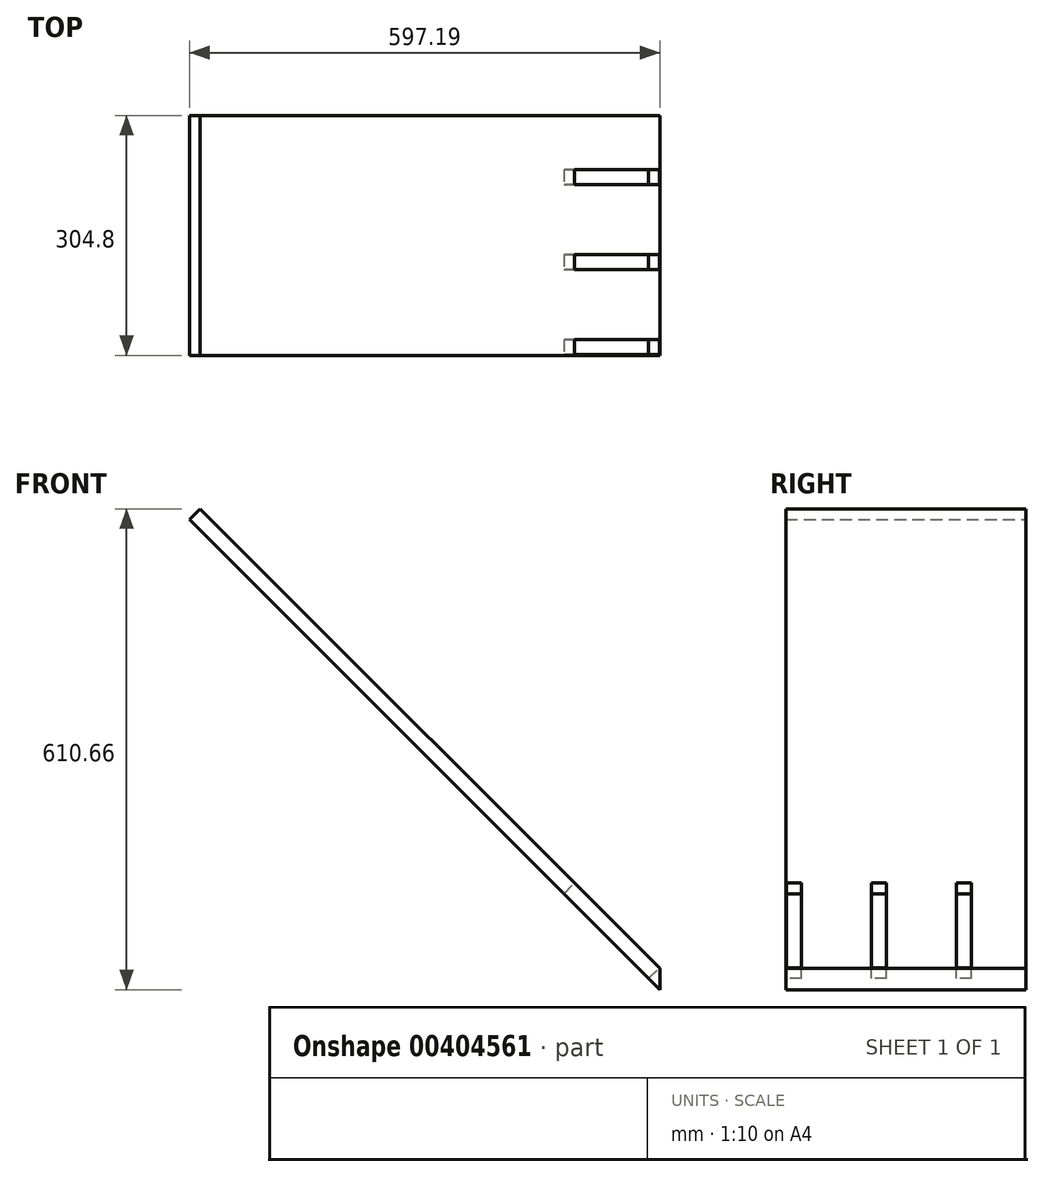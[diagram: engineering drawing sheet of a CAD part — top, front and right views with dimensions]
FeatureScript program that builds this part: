
annotation { "Feature Type Name" : "Feature", "Feature Type Description" : "" }
export const myFeature = defineFeature(function(context is Context, id is Id, definition is map)
    precondition{}
    {
        {
            var Q0;
            Q0=qCreatedBy(makeId("Front.planeOp"),FACE);
            var sketch = newSketch(context, id + "F0", { "sketchPlane" : qUnion([Q0])});
            skLineSegment(sketch, "E0.MirrorCS", {"start": v(378.53, 134.65) * mm, "end": v(-218.66, 731.84) * mm});
            skLineSegment(sketch, "E1.MirrorCS", {"start": v(378.53, 161.6) * mm, "end": v(-205.19, 745.3) * mm});
            skLineSegment(sketch, "E2.MirrorCS", {"start": v(378.53, 134.65) * mm, "end": v(378.53, 161.6) * mm});
            skLineSegment(sketch, "E3", {"start": v(-205.19, 745.3) * mm, "end": v(-218.66, 731.84) * mm});
            skSolve(sketch);
        }
        {
            var Q0;
            Q0=qSketchRegion(id+"F0",true);
            extrude(context, id + "F1", {"entities" : qUnion([Q0]), "endBound" : BoundingType.SYMMETRIC, "depth" : 304.8 * mm});
        }
        {
            var Q0;
            Q0=makeQuery(id+"F1.opExtrude","SWEPT_FACE",FACE,{"disambiguationData":[OSD([sQuery(id+"F0.wireOp",EDGE,"E1.MirrorCS")])]});
            var sketch = newSketch(context, id + "F2", { "sketchPlane" : qUnion([Q0])});
            skLineSegment(sketch, "E4.bottom", {"start": v(83.55, -152.4) * mm, "end": v(64.5, -152.4) * mm});
            skLineSegment(sketch, "E4.top", {"start": v(83.55, 0) * mm, "end": v(64.5, 0) * mm});
            skLineSegment(sketch, "E4.left", {"start": v(83.55, -152.4) * mm, "end": v(83.55, 0) * mm});
            skLineSegment(sketch, "E4.right", {"start": v(64.5, -152.4) * mm, "end": v(64.5, 0) * mm});
            skLineSegment(sketch, "E5.bottom", {"start": v(-24.4, -152.4) * mm, "end": v(-43.45, -152.4) * mm});
            skLineSegment(sketch, "E5.top", {"start": v(-24.4, 0) * mm, "end": v(-43.45, 0) * mm});
            skLineSegment(sketch, "E5.left", {"start": v(-24.4, -152.4) * mm, "end": v(-24.4, 0) * mm});
            skLineSegment(sketch, "E5.right", {"start": v(-43.45, -152.4) * mm, "end": v(-43.45, 0) * mm});
            skLineSegment(sketch, "E6.bottom", {"start": v(-132.35, -152.4) * mm, "end": v(-151.4, -152.4) * mm});
            skLineSegment(sketch, "E6.top", {"start": v(-132.35, 0) * mm, "end": v(-151.4, 0) * mm});
            skLineSegment(sketch, "E6.left", {"start": v(-132.35, -152.4) * mm, "end": v(-132.35, 0) * mm});
            skLineSegment(sketch, "E6.right", {"start": v(-151.4, -152.4) * mm, "end": v(-151.4, 0) * mm});
            skLineSegment(sketch, "E7.bottom", {"start": v(-240.3, -152.4) * mm, "end": v(-259.35, -152.4) * mm});
            skLineSegment(sketch, "E7.top", {"start": v(-240.3, 0) * mm, "end": v(-259.35, 0) * mm});
            skLineSegment(sketch, "E7.left", {"start": v(-240.3, -152.4) * mm, "end": v(-240.3, 0) * mm});
            skLineSegment(sketch, "E7.right", {"start": v(-259.35, -152.4) * mm, "end": v(-259.35, 0) * mm});
            skLineSegment(sketch, "E8.bottom", {"start": v(-348.25, -152.4) * mm, "end": v(-367.3, -152.4) * mm});
            skLineSegment(sketch, "E8.top", {"start": v(-348.25, 0) * mm, "end": v(-367.3, 0) * mm});
            skLineSegment(sketch, "E8.left", {"start": v(-348.25, -152.4) * mm, "end": v(-348.25, 0) * mm});
            skLineSegment(sketch, "E8.right", {"start": v(-367.3, -152.4) * mm, "end": v(-367.3, 0) * mm});
            skLineSegment(sketch, "E9.bottom", {"start": v(-456.2, -152.4) * mm, "end": v(-475.25, -152.4) * mm});
            skLineSegment(sketch, "E9.top", {"start": v(-456.2, 0) * mm, "end": v(-475.25, 0) * mm});
            skLineSegment(sketch, "E9.left", {"start": v(-456.2, -152.4) * mm, "end": v(-456.2, 0) * mm});
            skLineSegment(sketch, "E9.right", {"start": v(-475.25, -152.4) * mm, "end": v(-475.25, 0) * mm});
            skLineSegment(sketch, "E10.bottom", {"start": v(-564.15, -152.4) * mm, "end": v(-583.2, -152.4) * mm});
            skLineSegment(sketch, "E10.top", {"start": v(-564.15, 0) * mm, "end": v(-583.2, 0) * mm});
            skLineSegment(sketch, "E10.left", {"start": v(-564.15, -152.4) * mm, "end": v(-564.15, 0) * mm});
            skLineSegment(sketch, "E10.right", {"start": v(-583.2, -152.4) * mm, "end": v(-583.2, 0) * mm});
            skSolve(sketch);
        }
        {
            var Q0;
            Q0=qSketchRegion(id+"F2",true);
            extrude(context, id + "F3", {"entities" : qUnion([Q0]), "operationType" : NewBodyOperationType.REMOVE, "oppositeDirection" : true, "depth" : 19.05 * mm});
        }
    });
